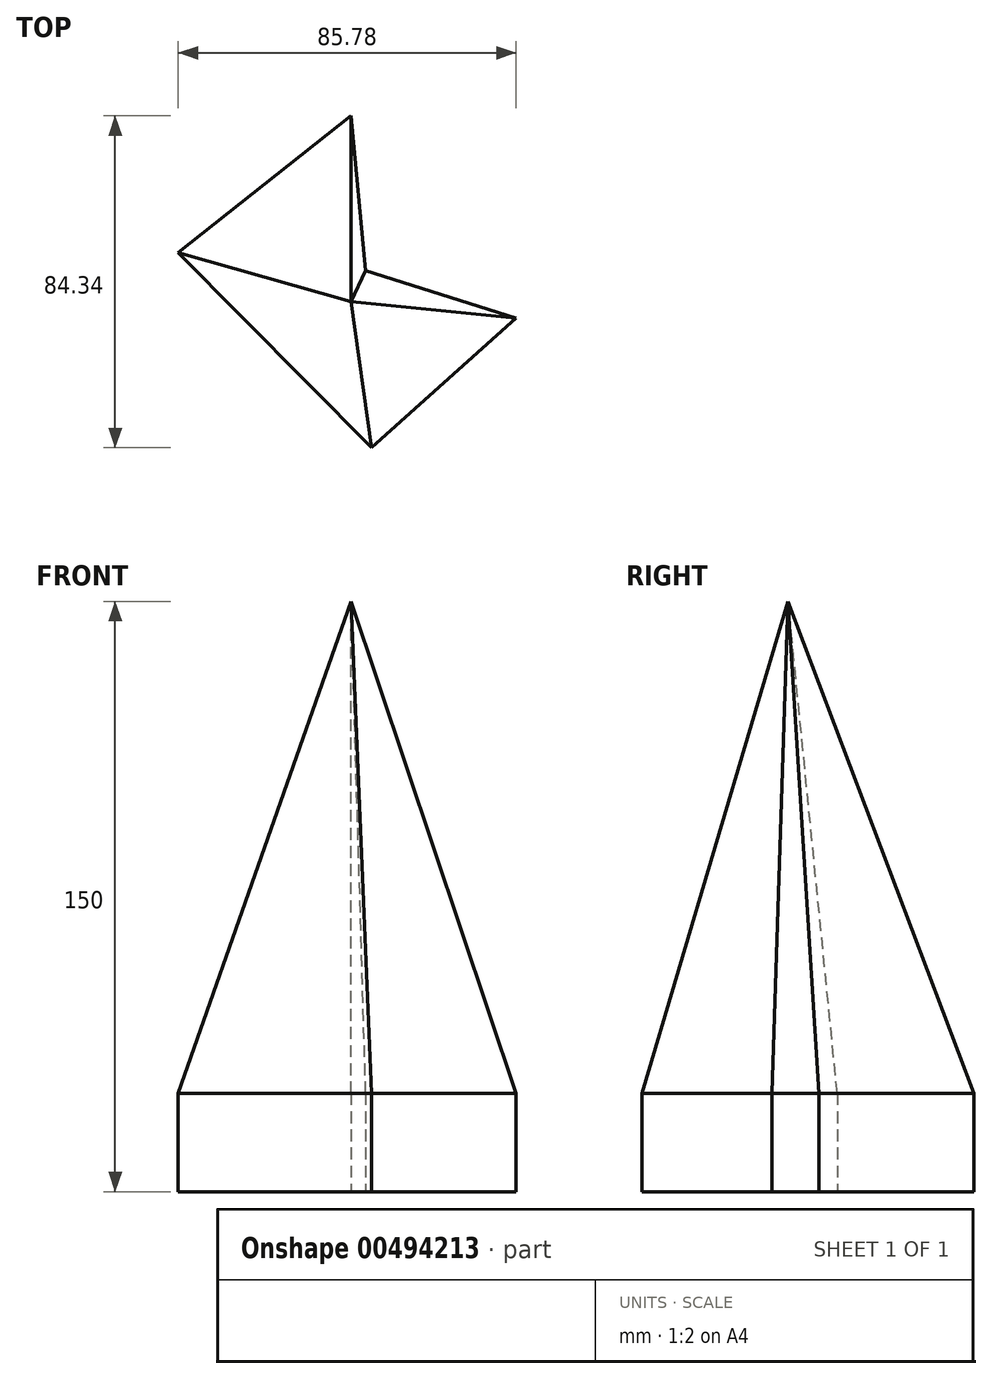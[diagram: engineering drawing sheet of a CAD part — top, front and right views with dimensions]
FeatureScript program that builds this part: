
annotation { "Feature Type Name" : "Feature", "Feature Type Description" : "" }
export const myFeature = defineFeature(function(context is Context, id is Id, definition is map)
    precondition{}
    {
        {
            var Q0;
            Q0=qCreatedBy(makeId("Top.planeOp"),FACE);
            var sketch = newSketch(context, id + "F0", { "sketchPlane" : qUnion([Q0])});
            skLineSegment(sketch, "E0", {"start": v(0, 47.2) * mm, "end": v(-43.9, 12.48) * mm});
            skLineSegment(sketch, "E1", {"start": v(-43.9, 12.48) * mm, "end": v(5.16, -37.15) * mm});
            skLineSegment(sketch, "E2", {"start": v(5.16, -37.15) * mm, "end": v(41.89, -4.16) * mm});
            skLineSegment(sketch, "E3", {"start": v(41.89, -4.16) * mm, "end": v(3.73, 7.89) * mm});
            skLineSegment(sketch, "E4", {"start": v(3.73, 7.89) * mm, "end": v(0, 47.2) * mm});
            skSolve(sketch);
        }
        {
            var Q0;
            Q0=makeQuery(id+"F0.imprint","IMPRINT",FACE,{"disambiguationData":[TD([[makeQuery(id+"F0.imprint","IMPRINT",EDGE,{"derivedFrom":sQuery(id+"F0.wireOp",EDGE,"E0")}),1.0]])]});
            extrude(context, id + "F1", {"entities" : qUnion([Q0]), "depth" : 25 * mm});
        }
        {
            var Q0;
            Q0=qCreatedBy(makeId("Top.planeOp"),FACE);
            cPlane(context, id + "F2", {"entities" : qUnion([Q0]), "cplaneType" : CPlaneType.OFFSET, "offset" : 150 * mm, "width" : 150 * mm, "height" : 150 * mm});
        }
        {
            var Q0;
            Q0=qCreatedBy(id+"F2.planeOp",FACE);
            var sketch = newSketch(context, id + "F3", { "sketchPlane" : qUnion([Q0])});
            skPoint(sketch, "E5", {"position": v(0, 0) * mm});
            skSolve(sketch);
        }
        {
            var Q1;
            Q1=makeQuery(id+"F1.opExtrude","CAP_FACE",FACE,{"disambiguationData":[OSD([sQuery(id+"F0.wireOp",EDGE,"E0"),sQuery(id+"F0.wireOp",EDGE,"E1"),sQuery(id+"F0.wireOp",EDGE,"E2"),sQuery(id+"F0.wireOp",EDGE,"E3"),sQuery(id+"F0.wireOp",EDGE,"E4")])],"isStart":false});
            var Q2;
            Q2=sQuery(id+"F3.wireOp",VERTEX,"E5");
            loft(context, id + "F4", {"operationType" : NewBodyOperationType.ADD, "sheetProfilesArray" : [{ "sheetProfileEntities" : qUnion([Q1]) }, { "sheetProfileEntities" : qUnion([Q2]) }]});
        }
    });
